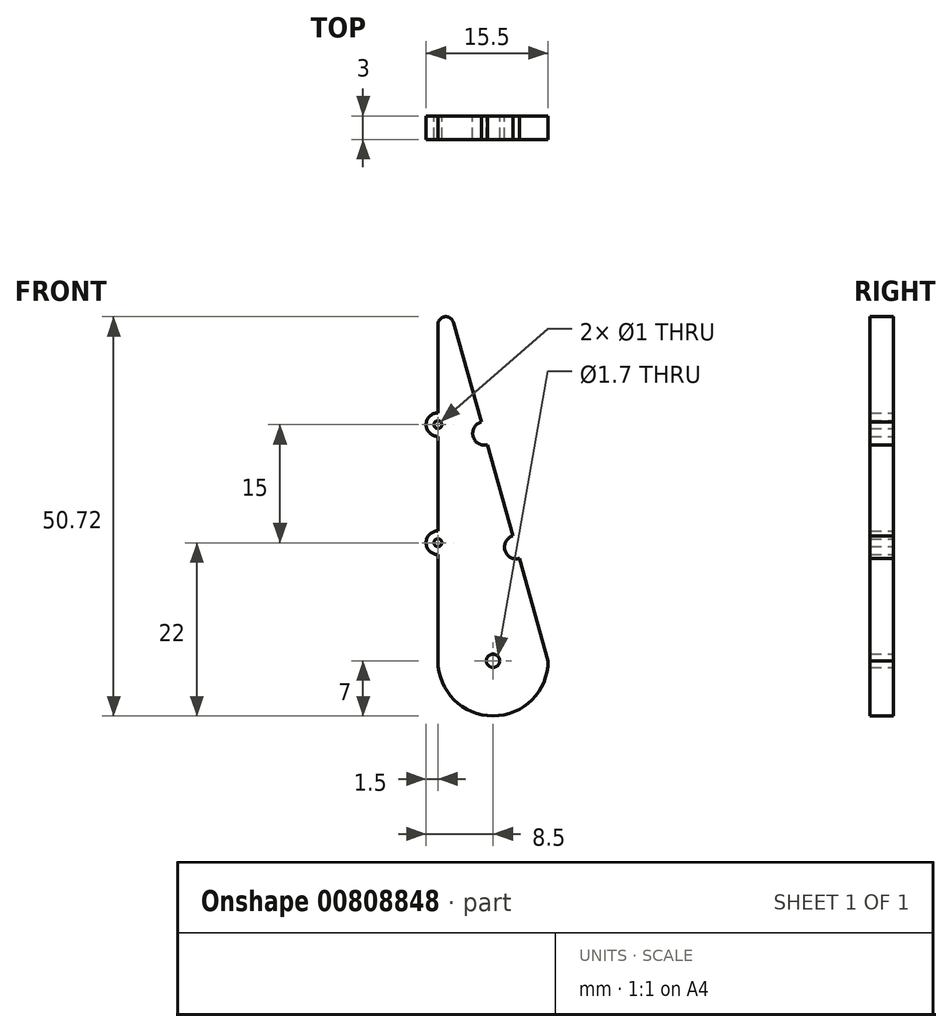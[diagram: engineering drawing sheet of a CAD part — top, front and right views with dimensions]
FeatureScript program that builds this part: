
annotation { "Feature Type Name" : "Feature", "Feature Type Description" : "" }
export const myFeature = defineFeature(function(context is Context, id is Id, definition is map)
    precondition{}
    {
        {
            var Q0;
            Q0=qCreatedBy(makeId("Front.planeOp"),FACE);
            var sketch = newSketch(context, id + "F0", { "sketchPlane" : qUnion([Q0])});
            skCircle(sketch, "E0", {"center": v(0, 0) * mm, "radius": 7 * mm});
            skLineSegment(sketch, "E1", {"start": v(-7, 0) * mm, "end": v(-7, 42.72) * mm});
            skLineSegment(sketch, "E2", {"start": v(7, 0) * mm, "end": v(-5.04, 42.99) * mm});
            skCircle(sketch, "E3", {"center": v(-7, 15) * mm, "radius": 1.5 * mm});
            skCircle(sketch, "E4", {"center": v(-7, 30) * mm, "radius": 1.5 * mm});
            skCircle(sketch, "E5", {"center": v(2.96, 14.44) * mm, "radius": 1.5 * mm});
            skCircle(sketch, "E6", {"center": v(-1.09, 28.89) * mm, "radius": 1.5 * mm});
            skCircle(sketch, "E7", {"center": v(2.96, 14.44) * mm, "radius": 0.5 * mm});
            skCircle(sketch, "E8", {"center": v(-7, 15) * mm, "radius": 0.5 * mm});
            skCircle(sketch, "E9", {"center": v(-7, 30) * mm, "radius": 0.5 * mm});
            skCircle(sketch, "E10", {"center": v(-1.09, 28.89) * mm, "radius": 0.5 * mm});
            skCircle(sketch, "E11", {"center": v(0, 0) * mm, "radius": 0.85 * mm});
            skPoint(sketch, "E12.visualSharp", {"position": v(-7, 50) * mm});
            skArc(sketch, "E12.filletArc", {"start": v(-5.04, 42.99) * mm, "mid": v(-6.14, 43.71) * mm, "end": v(-7, 42.72) * mm});
            skSolve(sketch);
        }
        {
            var Q0;
            {var subQ0=sQuery(id+"F0.wireOp",EDGE,"E3");var subQ1=sQuery(id+"F0.wireOp",EDGE,"E1");var subQ2=makeQuery(id+"F0.imprint","INTERSECT",VERTEX,{"disambiguationData":[OD(0.0)],"derivedFrom":[subQ1,subQ0]});Q0=makeQuery(id+"F0.imprint","IMPRINT",FACE,{"disambiguationData":[TD([[makeQuery(id+"F0.imprint","IMPRINT",EDGE,{"disambiguationData":[TD([[subQ2,-1.0]])],"derivedFrom":subQ1}),1.0]])]});}
            var Q1;
            {var subQ0=sQuery(id+"F0.wireOp",EDGE,"E4");var subQ1=sQuery(id+"F0.wireOp",EDGE,"E1");var subQ2=makeQuery(id+"F0.imprint","INTERSECT",VERTEX,{"disambiguationData":[OD(0.0)],"derivedFrom":[subQ1,subQ0]});Q1=makeQuery(id+"F0.imprint","IMPRINT",FACE,{"disambiguationData":[TD([[makeQuery(id+"F0.imprint","IMPRINT",EDGE,{"disambiguationData":[TD([[subQ2,-1.0]])],"derivedFrom":subQ1}),1.0]])]});}
            var Q2;
            {var subQ0=sQuery(id+"F0.wireOp",EDGE,"E5");var subQ1=sQuery(id+"F0.wireOp",EDGE,"E2");var subQ2=makeQuery(id+"F0.imprint","INTERSECT",VERTEX,{"disambiguationData":[OD(0.0)],"derivedFrom":[subQ1,subQ0]});Q2=makeQuery(id+"F0.imprint","IMPRINT",FACE,{"disambiguationData":[TD([[makeQuery(id+"F0.imprint","IMPRINT",EDGE,{"disambiguationData":[TD([[subQ2,-1.0]])],"derivedFrom":subQ1}),-1.0]])]});}
            var Q3;
            {var subQ0=sQuery(id+"F0.wireOp",EDGE,"E6");var subQ1=sQuery(id+"F0.wireOp",EDGE,"E2");var subQ2=makeQuery(id+"F0.imprint","INTERSECT",VERTEX,{"disambiguationData":[OD(0.0)],"derivedFrom":[subQ1,subQ0]});Q3=makeQuery(id+"F0.imprint","IMPRINT",FACE,{"disambiguationData":[TD([[makeQuery(id+"F0.imprint","IMPRINT",EDGE,{"disambiguationData":[TD([[subQ2,-1.0]])],"derivedFrom":subQ1}),-1.0]])]});}
            var Q4;
            Q4=makeQuery(id+"F0.imprint","IMPRINT",FACE,{"disambiguationData":[TD([[makeQuery(id+"F0.imprint","IMPRINT",EDGE,{"derivedFrom":sQuery(id+"F0.wireOp",EDGE,"E11")}),-1.0]])]});
            var Q5;
            {var subQ0=sQuery(id+"F0.wireOp",EDGE,"E3");var subQ1=sQuery(id+"F0.wireOp",EDGE,"E1");var subQ2=makeQuery(id+"F0.imprint","INTERSECT",VERTEX,{"disambiguationData":[OD(0.0)],"derivedFrom":[subQ1,subQ0]});Q5=makeQuery(id+"F0.imprint","IMPRINT",FACE,{"disambiguationData":[TD([[makeQuery(id+"F0.imprint","IMPRINT",EDGE,{"disambiguationData":[TD([[subQ2,-1.0]])],"derivedFrom":subQ1}),-1.0]])]});}
            var Q6;
            {var subQ0=sQuery(id+"F0.wireOp",EDGE,"E4");var subQ1=sQuery(id+"F0.wireOp",EDGE,"E1");var subQ2=makeQuery(id+"F0.imprint","INTERSECT",VERTEX,{"disambiguationData":[OD(0.0)],"derivedFrom":[subQ1,subQ0]});Q6=makeQuery(id+"F0.imprint","IMPRINT",FACE,{"disambiguationData":[TD([[makeQuery(id+"F0.imprint","IMPRINT",EDGE,{"disambiguationData":[TD([[subQ2,-1.0]])],"derivedFrom":subQ1}),-1.0]])]});}
            var Q7;
            {var subQ0=sQuery(id+"F0.wireOp",EDGE,"E5");var subQ1=sQuery(id+"F0.wireOp",EDGE,"E2");var subQ2=makeQuery(id+"F0.imprint","INTERSECT",VERTEX,{"disambiguationData":[OD(0.0)],"derivedFrom":[subQ1,subQ0]});Q7=makeQuery(id+"F0.imprint","IMPRINT",FACE,{"disambiguationData":[TD([[makeQuery(id+"F0.imprint","IMPRINT",EDGE,{"disambiguationData":[TD([[subQ2,-1.0]])],"derivedFrom":subQ1}),1.0]])]});}
            var Q8;
            {var subQ0=sQuery(id+"F0.wireOp",EDGE,"E6");var subQ1=sQuery(id+"F0.wireOp",EDGE,"E2");var subQ2=makeQuery(id+"F0.imprint","INTERSECT",VERTEX,{"disambiguationData":[OD(0.0)],"derivedFrom":[subQ1,subQ0]});Q8=makeQuery(id+"F0.imprint","IMPRINT",FACE,{"disambiguationData":[TD([[makeQuery(id+"F0.imprint","IMPRINT",EDGE,{"disambiguationData":[TD([[subQ2,-1.0]])],"derivedFrom":subQ1}),1.0]])]});}
            var Q9;
            {var subQ4=sQuery(id+"F0.wireOp",EDGE,"E1");var subQ5=sQuery(id+"F0.wireOp",EDGE,"E0");var subQ6=makeQuery(id+"F0.imprint","INTERSECT",VERTEX,{"derivedFrom":[subQ5,subQ4]});Q9=makeQuery(id+"F0.imprint","IMPRINT",FACE,{"disambiguationData":[TD([[makeQuery(id+"F0.imprint","IMPRINT",EDGE,{"disambiguationData":[TD([[subQ6,1.0]])],"derivedFrom":subQ5}),-1.0]])]});}
            extrude(context, id + "F1", {"entities" : qUnion([Q0, Q1, Q2, Q3, Q4, Q5, Q6, Q7, Q8, Q9]), "depth" : 3 * mm, "offsetDistance" : 25 * mm});
        }
    });
